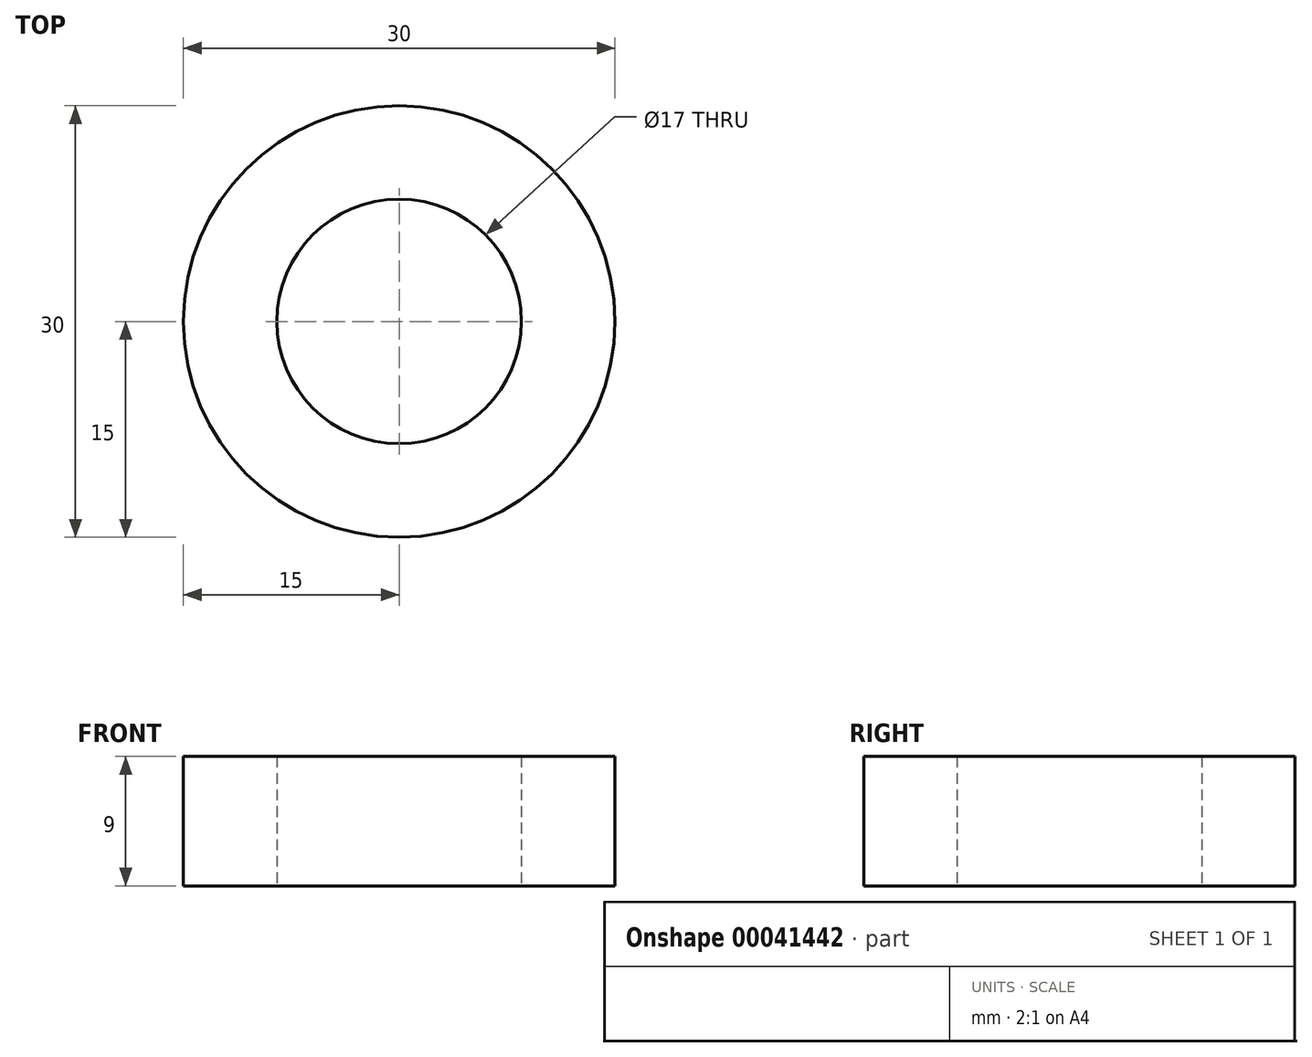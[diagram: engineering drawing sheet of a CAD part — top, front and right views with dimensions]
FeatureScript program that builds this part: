
annotation { "Feature Type Name" : "Feature", "Feature Type Description" : "" }
export const myFeature = defineFeature(function(context is Context, id is Id, definition is map)
    precondition{}
    {
        {
            var Q0;
            Q0=qCreatedBy(makeId("Top.planeOp"),FACE);
            var sketch = newSketch(context, id + "F0", { "sketchPlane" : qUnion([Q0])});
            skCircle(sketch, "E0", {"center": v(0, 0) * mm, "radius": 15 * mm});
            skCircle(sketch, "E1", {"center": v(0, 0) * mm, "radius": 8.5 * mm});
            skSolve(sketch);
        }
        {
            var Q0;
            Q0=makeQuery(id+"F0.imprint","IMPRINT",FACE,{"disambiguationData":[TD([[makeQuery(id+"F0.imprint","IMPRINT",EDGE,{"derivedFrom":sQuery(id+"F0.wireOp",EDGE,"E0")}),1.0]])]});
            extrude(context, id + "F1", {"entities" : qUnion([Q0]), "depth" : 9 * mm});
        }
    });
